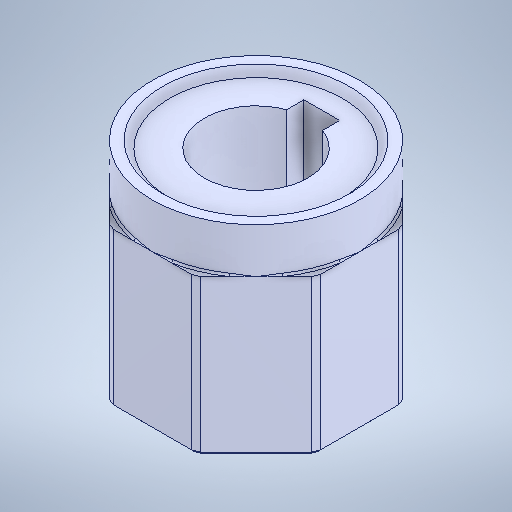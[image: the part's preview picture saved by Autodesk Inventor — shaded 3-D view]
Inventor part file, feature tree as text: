
AUTODESK INVENTOR PART (.ipt)
format: ipt  version: 2025.2 (Build 292293000, 293)  size: 375,808 bytes
history: native  units: mm
features: extrude x4, sketch x4, projected_geometry x1, fillet x1
ambient origin geometry x8: Origin, YZ Plane, XZ Plane, XY Plane, X Axis, Y Axis, Z Axis, Center Point
bodies: Solid1 (feature_tree)
feature tree (10):
  extrude  "Extrusion1"  Depth=10.0mm TaperAngle=0.0deg
  extrude  "Extrusion2"  TaperAngle=0.0deg  [1 undecoded]
  extrude  "Extrusion3"  Depth=10.0mm TaperAngle=0.0deg
  extrude  "Extrusion5"  [1 undecoded]
  sketch  "Sketch2"  dims[d0=18.0mm d1=10.0mm d2=0.0mm]
  sketch  "Sketch3"  dims[d3=15.0mm d4=0.0mm d5=0.0mm]
  sketch  "Sketch4"  dims[d6=4.2mm d7=10.0mm d8=0.0mm]
  sketch  "Sketch6"  dims[d11=5.0mm d12=0.0mm]
  projected_geometry  "Projected Loop2"
  fillet  "Fillet1"  [1 undecoded]
note: 3 required parameter values undecoded (feature->parameter linkage not recoverable at this tier; creation-order binding heuristic only, values carry confidence <= 0.55)
